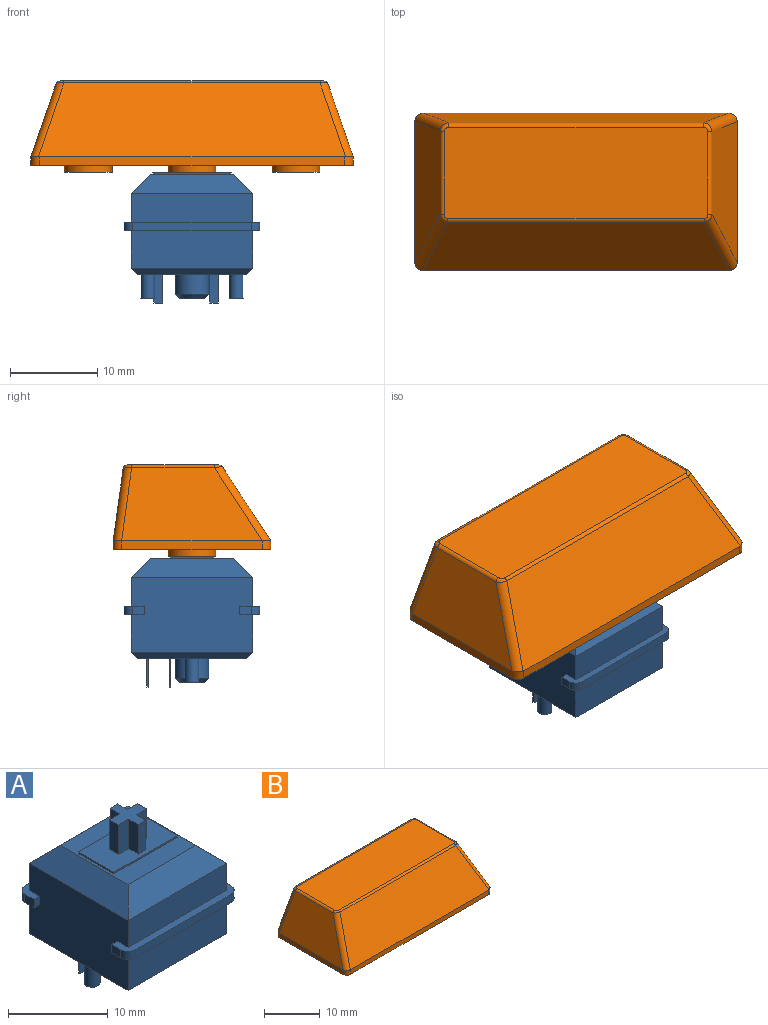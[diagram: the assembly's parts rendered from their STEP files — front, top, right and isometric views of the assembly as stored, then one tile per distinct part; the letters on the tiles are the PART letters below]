
ASSEMBLY  parts=2 mates=1
PART A: 69 faces, bbox 15.6x15.6x18.6 mm
  f0: plane 15.6x2.3mm, normal (0,0,-1), area 14.4mm2, adj f2,f3,f28,f30,f35,f60,f62,f63
  f1: plane 15.6x2.3mm, normal (0,0,-1), area 14.4mm2, adj f28,f30,f33,f34,f36,f59,f61,f64
  f2: plane 1.3x1mm, normal (1,0,0), area 1.3mm2, adj f0,f32,f62,f66
  f3: plane 1.3x1mm, normal (-1,0,0), area 1.3mm2, adj f0,f32,f63,f68
  f4: plane 15.6x2.3mm, normal (0,0,1), area 14.4mm2, adj f28,f30,f31,f33,f34,f36,f61,f64
  f5: plane 14x2.2mm, normal (-0.71,0,0.71), area 36.7mm2, adj f6,f7,f26,f30
  f6: plane 14x2.2mm, normal (0,-0.71,0.71), area 36.7mm2, adj f5,f7,f27,f31
  f7: plane 9.6x9.6mm, normal (0,0,1), area 47.2mm2, adj f5,f6,f8,f9,f10,f11,f26,f27
  f8: plane 5x0.2mm, normal (1,0,0), area 1mm2, adj f7,f9,f11,f12
  f9: plane 9x0.2mm, normal (0,1,0), area 1.8mm2, adj f7,f8,f10,f12
  f10: plane 5x0.2mm, normal (-1,0,0), area 1mm2, adj f7,f9,f11,f12
  f11: plane 9x0.2mm, normal (0,-1,0), area 1.8mm2, adj f7,f8,f10,f12
  f12: plane 9x5mm, normal (0,0,1), area 36.9mm2, adj f8,f9,f10,f11,f13,f14,f15,f16
  f13: plane 3.6x1.35mm, normal (1,0,0), area 4.9mm2, adj f12,f14,f24,f25
  f14: plane 3.6x1.08mm, normal (0,1,0), area 3.9mm2, adj f12,f13,f15,f25
  f15: plane 3.6x1.35mm, normal (-1,0,0), area 4.9mm2, adj f12,f14,f16,f25
  f16: plane 3.6x1.46mm, normal (0,1,0), area 5.3mm2, adj f12,f15,f17,f25
  f17: plane 3.6x1.3mm, normal (-1,0,0), area 4.7mm2, adj f12,f16,f18,f25
  f18: plane 3.6x1.46mm, normal (0,-1,0), area 5.3mm2, adj f12,f17,f19,f25
  f19: plane 3.6x1.35mm, normal (-1,0,0), area 4.9mm2, adj f12,f18,f20,f25
  f20: plane 3.6x1.08mm, normal (0,-1,0), area 3.9mm2, adj f12,f19,f21,f25
  f21: plane 3.6x1.35mm, normal (1,0,0), area 4.9mm2, adj f12,f20,f22,f25
  f22: plane 3.6x1.46mm, normal (0,-1,0), area 5.3mm2, adj f12,f21,f23,f25
  f23: plane 3.6x1.3mm, normal (1,0,0), area 4.7mm2, adj f12,f22,f24,f25
  f24: plane 3.6x1.46mm, normal (0,1,0), area 5.3mm2, adj f12,f13,f23,f25
  f25: plane 4x4mm, normal (0,0,1), area 8.1mm2, adj f13,f14,f15,f16,f17,f18,f19,f20
  f26: plane 14x2.2mm, normal (0,0.71,0.71), area 36.7mm2, adj f5,f7,f27,f29
  f27: plane 14x2.2mm, normal (0.71,0,0.71), area 36.7mm2, adj f6,f7,f26,f28
  f28: plane 14x8.6mm, normal (1,0,0), area 117.4mm2, adj f0,f1,f4,f27,f29,f31,f32,f55
  f29: plane 14x3.3mm, normal (0,1,0), area 46.2mm2, adj f26,f28,f30,f32
  f30: plane 14x8.6mm, normal (-1,0,0), area 117.4mm2, adj f0,f1,f4,f5,f29,f31,f32,f57
  f31: plane 14x3.3mm, normal (0,-1,0), area 46.2mm2, adj f4,f6,f28,f30
  f32: plane 15.6x2.3mm, normal (0,0,1), area 14.4mm2, adj f2,f3,f28,f29,f30,f35,f62,f63
  f33: plane 13.6x1mm, normal (0,-1,0), area 13.6mm2, adj f1,f4,f61,f64
  f34: plane 1.3x1mm, normal (1,0,0), area 1.3mm2, adj f1,f4,f61,f65
  f35: plane 13.6x1mm, normal (0,1,0), area 13.6mm2, adj f0,f32,f62,f63
  f36: plane 1.3x1mm, normal (-1,0,0), area 1.3mm2, adj f1,f4,f64,f67
  f37: plane 2.85x2.85mm, normal (0,0,-1), area 6.4mm2, adj f38
  f38: cone r=1.43mm half-angle=45deg, axis (0,0,1), area 7.4mm2, adj f37,f43
  f39: plane 1x0.2mm, normal (0,0,-1), area 0.2mm2, adj f44,f45,f46,f47
  f40: plane 1x0.2mm, normal (0,0,-1), area 0.2mm2, adj f48,f49,f50,f51
  f41: plane 1.6x1.6mm, normal (0,0,-1), area 2mm2, adj f52
  f42: plane 1.6x1.6mm, normal (0,0,-1), area 2mm2, adj f53
  f43: cylinder r=1.93mm len=3.85mm, axis (0,0,1), area 27.8mm2, adj f38,f54
  f44: plane 3.3x0.2mm, normal (-1,0,0), area 0.7mm2, adj f39,f45,f47,f54
  f45: plane 3.3x1mm, normal (0,1,0), area 3.3mm2, adj f39,f44,f46,f54
  f46: plane 3.3x0.2mm, normal (1,0,0), area 0.7mm2, adj f39,f45,f47,f54
  f47: plane 3.3x1mm, normal (0,-1,0), area 3.3mm2, adj f39,f44,f46,f54
  f48: plane 3.3x0.2mm, normal (-1,0,0), area 0.7mm2, adj f40,f49,f51,f54
  f49: plane 3.3x1mm, normal (0,1,0), area 3.3mm2, adj f40,f48,f50,f54
  f50: plane 3.3x0.2mm, normal (1,0,0), area 0.7mm2, adj f40,f49,f51,f54
  f51: plane 3.3x1mm, normal (0,-1,0), area 3.3mm2, adj f40,f48,f50,f54
  f52: cylinder r=0.8mm len=2.8mm, axis (0,0,1), area 14.1mm2, adj f41,f54
  f53: cylinder r=0.8mm len=2.8mm, axis (0,0,1), area 14.1mm2, adj f42,f54
  f54: plane 12.6x12.6mm, normal (0,0,-1), area 142.7mm2, adj f43,f44,f45,f46,f47,f48,f49,f50
  f55: plane 14x0.7mm, normal (0.71,0,-0.71), area 13.2mm2, adj f28,f54,f56,f58
  f56: plane 14x0.7mm, normal (0,0.71,-0.71), area 13.2mm2, adj f54,f55,f57,f60
  f57: plane 14x0.7mm, normal (-0.71,0,-0.71), area 13.2mm2, adj f30,f54,f56,f58
  f58: plane 14x0.7mm, normal (0,-0.71,-0.71), area 13.2mm2, adj f54,f55,f57,f59
  f59: plane 14x4.3mm, normal (0,-1,0), area 60.2mm2, adj f1,f28,f30,f58
  f60: plane 14x4.3mm, normal (0,1,0), area 60.2mm2, adj f0,f28,f30,f56
  f61: cylinder r=1mm len=1mm, axis (0,0,-1), area 1.6mm2, adj f1,f4,f33,f34
  f62: cylinder r=1mm len=1mm, axis (0,0,1), area 1.6mm2, adj f0,f2,f32,f35
  f63: cylinder r=1mm len=1mm, axis (0,0,-1), area 1.6mm2, adj f0,f3,f32,f35
  f64: cylinder r=1mm len=1mm, axis (0,0,1), area 1.6mm2, adj f1,f4,f33,f36
  f65: plane 1x0.8mm, normal (0,1,0), area 0.8mm2, adj f1,f4,f28,f34
  f66: plane 1x0.8mm, normal (0,-1,0), area 0.8mm2, adj f0,f2,f28,f32
  f67: plane 1x0.8mm, normal (0,1,0), area 0.8mm2, adj f1,f4,f30,f36
  f68: plane 1x0.8mm, normal (0,-1,0), area 0.8mm2, adj f0,f3,f30,f32
PART B: 80 faces, bbox 37.2x18.1x10.5 mm
  f0: plane 37x18.1mm, normal (0,0,-1), area 105.3mm2, adj f1,f2,f3,f4,f10,f12,f14,f16
  f1: plane 35x1mm, normal (0,-1,0), area 35mm2, adj f0,f8,f10,f12
  f2: plane 16.1x1mm, normal (1,0,0), area 16.1mm2, adj f0,f9,f10,f16
  f3: plane 35x1mm, normal (0,1,0), area 35mm2, adj f0,f6,f14,f15,f16,f17
  f4: plane 16.1x1mm, normal (-1,0,0), area 16.1mm2, adj f0,f7,f12,f14
  f5: plane 30.29x10.49mm, normal (0,0,1), area 317.6mm2, adj f18,f19,f20,f21,f22,f23,f24,f25
  f6: plane 34.98x8.27mm, normal (0,0.99,0.14), area 268.2mm2, adj f3,f15,f17,f20
  f7: plane 16.15x8.36mm, normal (-0.95,0,0.33), area 113.6mm2, adj f4,f12,f13,f14,f15,f19
  f8: plane 35.26x8.48mm, normal (0,-0.84,0.55), area 327.6mm2, adj f1,f10,f11,f12,f13,f23
  f9: plane 16.15x8.36mm, normal (0.95,0,0.33), area 113.6mm2, adj f2,f10,f11,f16,f17,f24
  f10: cylinder r=1mm len=1.07mm, axis (0,0,1), area 1.6mm2, adj f0,f1,f2,f8,f9,f11
  f11: cylinder r=1mm len=8.85mm, axis (-0.28,0.53,0.8), area 14.6mm2, adj f8,f9,f10,f25
  f12: cylinder r=1mm len=1.07mm, axis (0,0,-1), area 1.6mm2, adj f0,f1,f4,f7,f8,f13
  f13: cylinder r=1mm len=8.85mm, axis (-0.28,-0.53,-0.8), area 14.6mm2, adj f7,f8,f12,f21
  f14: cylinder r=1mm len=1.03mm, axis (0,0,1), area 1.6mm2, adj f0,f3,f4,f7,f15
  f15: cylinder r=1mm len=8.67mm, axis (0.32,-0.13,0.94), area 13.6mm2, adj f3,f6,f7,f14,f18
  f16: cylinder r=1mm len=1.03mm, axis (0,0,-1), area 1.6mm2, adj f0,f2,f3,f9,f17
  f17: cylinder r=1mm len=8.67mm, axis (0.32,0.13,-0.94), area 13.6mm2, adj f3,f6,f9,f16,f22
  f18: bspline ~1.06x1.03mm, area 0.8mm2, adj f5,f15,f19,f20
  f19: cylinder r=0.5mm len=9.52mm, axis (0,-1,0), area 5.9mm2, adj f5,f7,f18,f21
  f20: cylinder r=0.5mm len=29.28mm, axis (-1,0,0), area 21mm2, adj f5,f6,f18,f22
  f21: bspline ~0.91x0.91mm, area 0.6mm2, adj f5,f13,f19,f23
  f22: bspline ~0.99x0.98mm, area 0.8mm2, adj f5,f17,f20,f24
  f23: cylinder r=0.5mm len=29.42mm, axis (-1,0,0), area 14.6mm2, adj f5,f8,f21,f25
  f24: cylinder r=0.5mm len=9.52mm, axis (0,-1,0), area 5.9mm2, adj f5,f9,f22,f25
  f25: bspline ~0.91x0.91mm, area 0.6mm2, adj f5,f11,f23,f24
  f26: plane 35x0.7mm, normal (0,1,0), area 24.6mm2, adj f0,f27,f29,f33
  f27: plane 16.1x0.83mm, normal (-1,0,0), area 13.4mm2, adj f0,f26,f28,f33,f34
  f28: plane 35x0.93mm, normal (0,-1,0), area 32.6mm2, adj f0,f27,f29,f31,f32,f34
  f29: plane 16.1x0.83mm, normal (1,0,0), area 13.4mm2, adj f0,f26,f28,f32,f33
  f30: plane 29.57x9.79mm, normal (0,0,-1), area 218.2mm2, adj f31,f32,f33,f34,f46,f61,f76
  f31: plane 34.93x7.77mm, normal (0,-0.99,-0.14), area 252.9mm2, adj f28,f30,f32,f34
  f32: plane 16.01x7.87mm, normal (0.95,0,-0.33), area 107.4mm2, adj f28,f29,f30,f31,f33
  f33: plane 35x8mm, normal (0,0.84,-0.55), area 309.2mm2, adj f26,f27,f29,f30,f32,f34
  f34: plane 16.01x7.87mm, normal (-0.95,0,-0.33), area 107.4mm2, adj f27,f28,f30,f31,f33
  f35: plane 9.5x1.5mm, normal (0,1,0), area 14.2mm2, adj f36,f44,f45,f49
  f36: plane 9.5x1.3mm, normal (1,0,0), area 12.3mm2, adj f35,f37,f45,f49
  f37: plane 9.5x1.5mm, normal (0,-1,0), area 14.2mm2, adj f36,f38,f45,f49
  f38: plane 9.5x1.35mm, normal (1,0,0), area 12.8mm2, adj f37,f39,f45,f49
  f39: plane 9.5x1mm, normal (0,-1,0), area 9.5mm2, adj f38,f40,f45,f49
  f40: plane 9.5x1.35mm, normal (-1,0,0), area 12.8mm2, adj f39,f41,f45,f49
  f41: plane 9.5x1.5mm, normal (0,-1,0), area 14.2mm2, adj f40,f42,f45,f49
  f42: plane 9.5x1.3mm, normal (-1,0,0), area 12.3mm2, adj f41,f43,f45,f49
  f43: plane 9.5x1.5mm, normal (0,1,0), area 14.2mm2, adj f42,f45,f47,f49
  f44: plane 9.5x1.35mm, normal (1,0,0), area 12.8mm2, adj f35,f45,f48,f49
  f45: plane 5.5x5.5mm, normal (0,0,-1), area 15.9mm2, adj f35,f36,f37,f38,f39,f40,f41,f42
  f46: cylinder r=2.75mm len=9.5mm, axis (0,0,-1), area 164.1mm2, adj f30,f45
  f47: plane 9.5x1.35mm, normal (-1,0,0), area 12.8mm2, adj f43,f45,f48,f49
  f48: plane 9.5x1mm, normal (0,1,0), area 9.5mm2, adj f44,f45,f47,f49
  f49: plane 4x4mm, normal (0,0,-1), area 7.9mm2, adj f35,f36,f37,f38,f39,f40,f41,f42
  f50: plane 9.5x1.3mm, normal (-1,0,0), area 12.3mm2, adj f51,f59,f60,f64
  f51: plane 9.5x1.5mm, normal (0,1,0), area 14.3mm2, adj f50,f52,f60,f64
  f52: plane 9.5x1.35mm, normal (-1,0,0), area 12.8mm2, adj f51,f53,f60,f64
  f53: plane 9.5x1mm, normal (0,1,0), area 9.5mm2, adj f52,f54,f60,f64
  f54: plane 9.5x1.35mm, normal (1,0,0), area 12.8mm2, adj f53,f55,f60,f64
  f55: plane 9.5x1.5mm, normal (0,1,0), area 14.2mm2, adj f54,f56,f60,f64
  f56: plane 9.5x1.3mm, normal (1,0,0), area 12.3mm2, adj f55,f57,f60,f64
  f57: plane 9.5x1.5mm, normal (0,-1,0), area 14.2mm2, adj f56,f58,f60,f64
  f58: plane 9.5x1.35mm, normal (1,0,0), area 12.8mm2, adj f57,f60,f62,f64
  f59: plane 9.5x1.5mm, normal (0,-1,0), area 14.3mm2, adj f50,f60,f63,f64
  f60: plane 5.5x5.5mm, normal (0,0,-1), area 15.9mm2, adj f50,f51,f52,f53,f54,f55,f56,f57
  f61: cylinder r=2.75mm len=9.5mm, axis (0,0,-1), area 164.1mm2, adj f30,f60
  f62: plane 9.5x1mm, normal (0,-1,0), area 9.5mm2, adj f58,f60,f63,f64
  f63: plane 9.5x1.35mm, normal (-1,0,0), area 12.8mm2, adj f59,f60,f62,f64
  f64: plane 4x4mm, normal (0,0,-1), area 7.9mm2, adj f50,f51,f52,f53,f54,f55,f56,f57
  f65: plane 9.5x1.3mm, normal (-1,0,0), area 12.3mm2, adj f66,f74,f75,f79
  f66: plane 9.5x1.5mm, normal (0,1,0), area 14.2mm2, adj f65,f67,f75,f79
  f67: plane 9.5x1.35mm, normal (-1,0,0), area 12.8mm2, adj f66,f68,f75,f79
  f68: plane 9.5x1mm, normal (0,1,0), area 9.5mm2, adj f67,f69,f75,f79
  f69: plane 9.5x1.35mm, normal (1,0,0), area 12.8mm2, adj f68,f70,f75,f79
  f70: plane 9.5x1.5mm, normal (0,1,0), area 14.3mm2, adj f69,f71,f75,f79
  f71: plane 9.5x1.3mm, normal (1,0,0), area 12.3mm2, adj f70,f72,f75,f79
  f72: plane 9.5x1.5mm, normal (0,-1,0), area 14.3mm2, adj f71,f73,f75,f79
  f73: plane 9.5x1.35mm, normal (1,0,0), area 12.8mm2, adj f72,f75,f77,f79
  f74: plane 9.5x1.5mm, normal (0,-1,0), area 14.2mm2, adj f65,f75,f78,f79
  f75: plane 5.5x5.5mm, normal (0,0,-1), area 15.9mm2, adj f65,f66,f67,f68,f69,f70,f71,f72
  f76: cylinder r=2.75mm len=9.5mm, axis (0,0,-1), area 164.1mm2, adj f30,f75
  f77: plane 9.5x1mm, normal (0,-1,0), area 9.5mm2, adj f73,f75,f78,f79
  f78: plane 9.5x1.35mm, normal (-1,0,0), area 12.8mm2, adj f74,f75,f77,f79
  f79: plane 4x4mm, normal (0,0,-1), area 7.9mm2, adj f65,f66,f67,f68,f69,f70,f71,f72
PLACE A at identity fixed
PLACE B t=(0,0,11.7)mm
MATE fastened B.f46 <-> A.f38  axis (0,0,-1) through (0,0,11.7)mm
